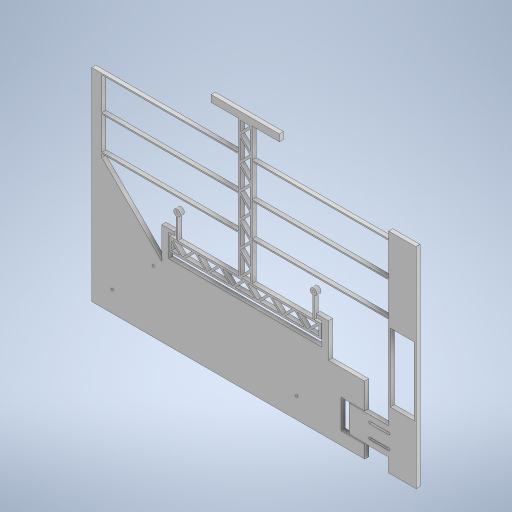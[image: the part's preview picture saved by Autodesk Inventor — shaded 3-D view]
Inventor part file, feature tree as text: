
AUTODESK INVENTOR PART (.ipt)
format: ipt  version: 2023 (Build 270158000, 158)  size: 690,176 bytes
history: native  units: mm
features: extrude x8, sketch x8, other x4, reference x2, projected_geometry x1
ambient origin geometry x8: Origin, YZ Plane, XZ Plane, XY Plane, X Axis, Y Axis, Z Axis, Center Point
bodies: Solid1 (feature_tree)
feature tree (23):
  other  "<userpath>\ClawdDrive\Objet3D\IminaProbe\RoueMDF\Settings.xlsx"
  extrude  "Extrusion1"  Depth=350.0mm
  extrude  "Extrusion2"  TaperAngle=45.0deg  [1 undecoded]
  extrude  "Extrusion3"  Depth=100.0mm
  extrude  "Extrusion4"  Depth=3.0mm
  extrude  "Extrusion6"  Depth=10.0mm
  extrude  "Extrusion7"  Depth=2.0mm
  extrude  "Extrusion8"  Depth=30.0mm
  extrude  "Extrusion5"  Depth=20.0mm
  sketch  "Sketch1"  dims[d0=420.0mm d1=350.0mm]
  sketch  "Sketch2"  dims[d2=45.0deg d3=45.0deg]
  reference  "Reference1"
  sketch  "Sketch3"  dims[d4=100.0mm d5=100.0mm]
  sketch  "Sketch4"  dims[d6=3.0mm d7=3.0mm]
  reference  "Reference2"
  sketch  "Sketch5"  dims[d8=10.0mm d9=10.0mm]
  projected_geometry  "Projected Loop1"
  sketch  "Sketch6"  dims[d10=1.0mm d11=2.0mm]
  sketch  "Sketch7"  dims[d12=30.0mm d13=30.0mm]
  sketch  "Sketch8"  dims[d14=2.0mm d15=20.0mm d16=10.0mm d17=10.0mm d23=10.0mm d24=10.0mm d25=10.0mm d26=200.0mm d28=2.0mm d29=200.0mm d30=2.0mm d31=200.0mm d32=100.0mm d33=20.0mm d34=10.0mm d35=40.0mm d36=40.0mm d37=200.0mm d38=200.0mm d39=2.0mm d40=2.0mm d41=100.0mm d42=2.0mm d43=50.0mm d44=40.0mm d45=10.0mm d46=10.0mm d47=50.0mm d48=100.0mm d49=2.5mm d50=2.5mm d52=6.0mm d53=0.0mm d54=1.0mm d55=1.0mm d56=40.0mm d57=12.0mm d58=20.0mm d59=6.0mm d60=0.0mm d61=45.0deg d62=6.0mm d63=0.0mm d64=6.0mm d65=0.0mm d66=9.0mm d67=10.0mm d68=0.0mm d69=2.0mm d70=475.0mm d71=6.0mm d72=0.0mm d73=30.0mm d74=20.0mm d75=3.0mm d76=3.0mm d77=40.0mm d78=30.0mm d79=3.0mm d80=3.0mm d81=30.0mm d82=30.0mm d83=6.0mm d84=0.0mm d85=3.0mm d86=3.0mm d87=3.0mm d88=3.0mm d89=3.0mm d90=1.5mm d91=45.0deg d92=3.0mm d93=3.0mm d94=36.485281mm d95=60.0mm d97=36.485281mm d98=10.0mm d100=10.0mm d102=3.0mm d103=3.0mm d104=3.0mm d105=3.0mm d106=3.0mm d107=1.5mm d108=45.0deg d109=3.0mm d110=3.0mm d111=36.485281mm d112=50.0mm d114=36.485281mm d115=10.0mm d117=10.0mm d119=10.0mm d120=0.0mm d121=0.0mm d122=0.0mm d123=10.0mm d124=10.0mm d125=1.0mm d126=1.0mm d127=5.0mm d128=4.0mm d129=5.0mm d130=3.0mm d131=3.0mm d132=4.0mm]
  other  "<userpath>\ClawdDrive\Objet3D\IminaProbe\RoueMDF\Assembly1.iam"
  other  "Assembly1.iam"
  other  "Wheel1:1"
note: 1 required parameter value undecoded (feature->parameter linkage not recoverable at this tier; creation-order binding heuristic only, values carry confidence <= 0.55)
